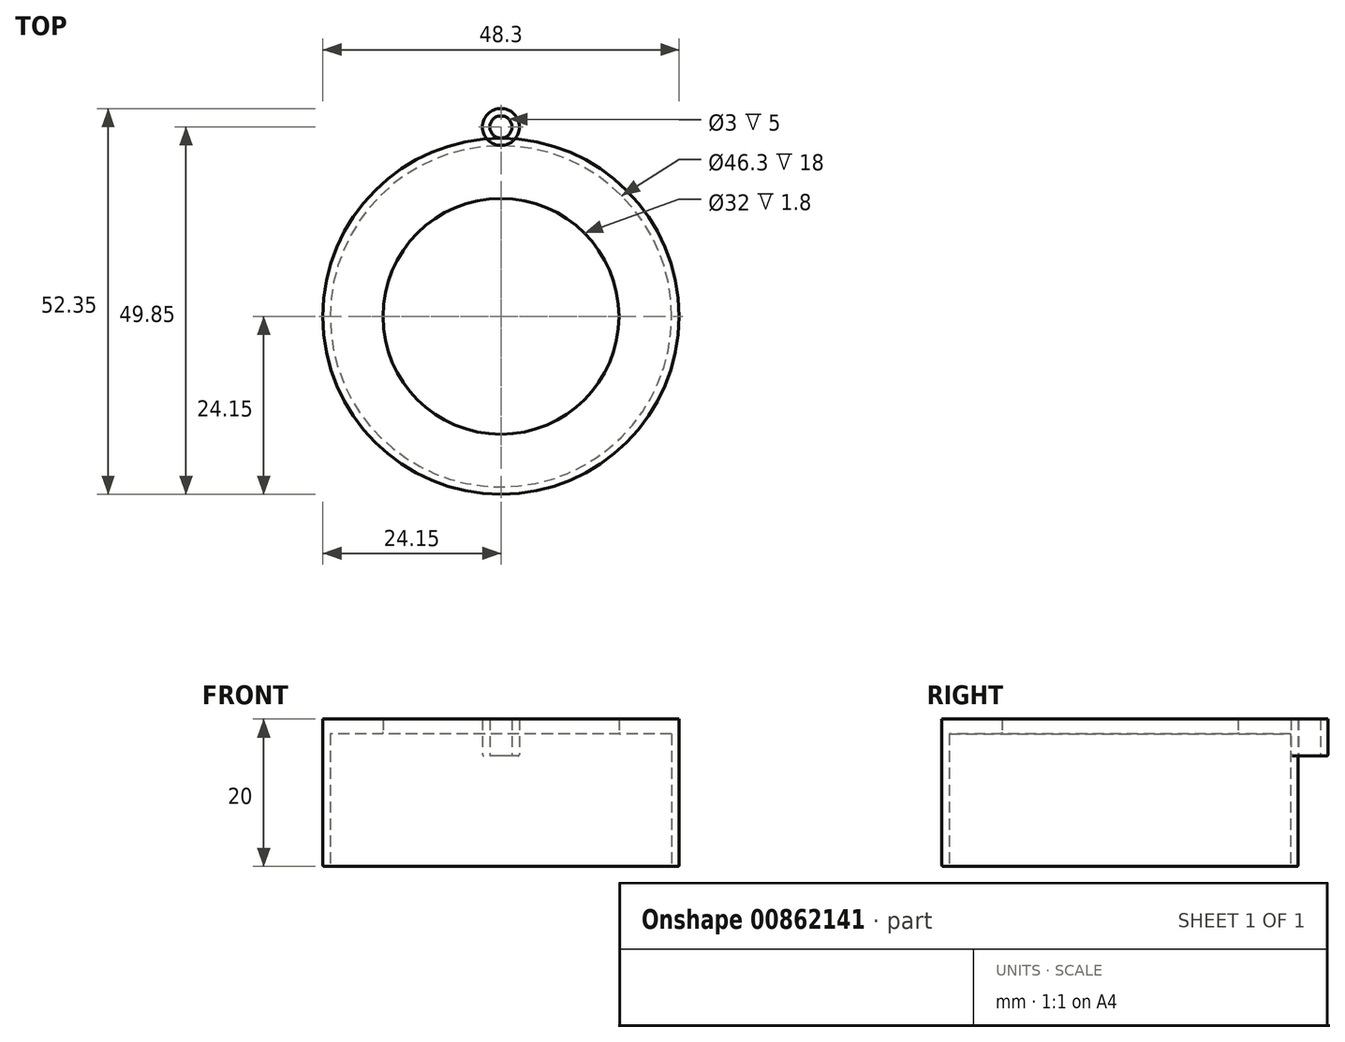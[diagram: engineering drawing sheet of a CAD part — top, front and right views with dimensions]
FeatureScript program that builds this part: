
annotation { "Feature Type Name" : "Feature", "Feature Type Description" : "" }
export const myFeature = defineFeature(function(context is Context, id is Id, definition is map)
    precondition{}
    {
        {
            var Q0;
            Q0=qCreatedBy(makeId("Top.planeOp"),FACE);
            var sketch = newSketch(context, id + "F0", { "sketchPlane" : qUnion([Q0])});
            skCircle(sketch, "E0", {"center": v(0, 0) * mm, "radius": 24.15 * mm});
            skSolve(sketch);
        }
        {
            var Q0;
            Q0 = qSketchRegion(id + "F0", true);
            extrude(context, id + "F1", {"entities" : qUnion([Q0]), "depth" : 20 * mm, "offsetDistance" : 25 * mm});
        }
        {
            var Q0;
            Q0=qCreatedBy(makeId("Top.planeOp"),FACE);
            var sketch = newSketch(context, id + "F2", { "sketchPlane" : qUnion([Q0])});
            skCircle(sketch, "E1", {"center": v(0, 0) * mm, "radius": 23.15 * mm});
            skSolve(sketch);
        }
        {
            var Q0;
            Q0 = qSketchRegion(id + "F2", true);
            extrude(context, id + "F3", {"entities" : qUnion([Q0]), "operationType" : NewBodyOperationType.REMOVE, "depth" : 18 * mm, "offsetDistance" : 25 * mm});
        }
        {
            var Q0;
            Q0=qCreatedBy(makeId("Top.planeOp"),FACE);
            var sketch = newSketch(context, id + "F4", { "sketchPlane" : qUnion([Q0])});
            skCircle(sketch, "E2", {"center": v(0, 0) * mm, "radius": 16 * mm});
            skSolve(sketch);
        }
        {
            var Q0;
            Q0 = qSketchRegion(id + "F4", true);
            extrude(context, id + "F5", {"entities" : qUnion([Q0]), "operationType" : NewBodyOperationType.REMOVE, "depth" : 20 * mm, "offsetDistance" : 25 * mm});
        }
        {
            var Q0;
            Q0=qCreatedBy(makeId("Top.planeOp"),FACE);
            var sketch = newSketch(context, id + "F6", { "sketchPlane" : qUnion([Q0])});
            skCircle(sketch, "E3", {"center": v(0, 0) * mm, "radius": 2.5 * mm});
            skSolve(sketch);
        }
        {
            var Q0;
            Q0 = qSketchRegion(id + "F6", true);
            extrude(context, id + "F7", {"entities" : qUnion([Q0]), "depth" : 5 * mm, "offsetDistance" : 25 * mm});
        }
        {
            var Q0;
            Q0=qCreatedBy(makeId("Top.planeOp"),FACE);
            var sketch = newSketch(context, id + "F8", { "sketchPlane" : qUnion([Q0])});
            skCircle(sketch, "E4", {"center": v(0, 0) * mm, "radius": 1.5 * mm});
            skSolve(sketch);
        }
        {
            var Q0;
            Q0 = qSketchRegion(id + "F8", true);
            extrude(context, id + "F9", {"entities" : qUnion([Q0]), "operationType" : NewBodyOperationType.REMOVE, "depth" : 5 * mm, "offsetDistance" : 25 * mm});
        }
        {
            var Q0;
            Q0=makeQuery(id+"F7.opExtrude","SWEPT_BODY",BODY,{"disambiguationData":[OSD([sQuery(id+"F6.wireOp",EDGE,"E3")])]});
            transform(context, id + "F10", {"entities" : qUnion([Q0]), "transformType" : TransformType.TRANSLATION_3D, "dx" : 0 * mm, "dy" : 25.6 * mm, "dz" : 15 * mm, "makeCopy" : false});
        }
        {
            var Q0;
            Q0=makeQuery(id+"F1.opExtrude","CAP_EDGE",EDGE,{"disambiguationData":[OSD([sQuery(id+"F0.wireOp",EDGE,"E0")])],"isStart":true});
            var Q1;
            Q1=makeQuery(id+"F3.boolean.opBoolean","COPY",EDGE,{"derivedFrom":makeQuery(id+"F3.opExtrude","CAP_EDGE",EDGE,{"disambiguationData":[OSD([sQuery(id+"F2.wireOp",EDGE,"E1")])],"isStart":true})});
            var Q2;
            Q2=makeQuery(id+"F5.boolean.opBoolean","INTERSECT",EDGE,{"derivedFrom":[makeQuery(id+"F3.boolean.opBoolean","COPY",FACE,{"derivedFrom":makeQuery(id+"F3.opExtrude","CAP_FACE",FACE,{"disambiguationData":[OSD([sQuery(id+"F2.wireOp",EDGE,"E1")])],"isStart":false})}),makeQuery(id+"F5.opExtrude","SWEPT_FACE",FACE,{"disambiguationData":[OSD([sQuery(id+"F4.wireOp",EDGE,"E2")])]})]});
            var Q3;
            Q3=makeQuery(id+"F7.opExtrude","CAP_EDGE",EDGE,{"disambiguationData":[OSD([sQuery(id+"F6.wireOp",EDGE,"E3")])],"isStart":true});
            var Q4;
            Q4=makeQuery(id+"F9.boolean.opBoolean","COPY",EDGE,{"derivedFrom":makeQuery(id+"F9.opExtrude","CAP_EDGE",EDGE,{"disambiguationData":[OSD([sQuery(id+"F8.wireOp",EDGE,"E4")])],"isStart":true})});
            fillet(context, id + "F11", {"entities" : qUnion([Q0, Q1, Q2, Q3, Q4]), "radius" : 0.2 * mm, "tangentPropagation" : true, "allowEdgeOverflow" : false});
        }
        {
            var Q0;
            Q0=makeQuery(id+"F7.opExtrude","SWEPT_BODY",BODY,{"disambiguationData":[OSD([sQuery(id+"F6.wireOp",EDGE,"E3")])]});
            transform(context, id + "F12", {"entities" : qUnion([Q0]), "transformType" : TransformType.TRANSLATION_3D, "dx" : 0 * mm, "dy" : 0.1 * mm, "dz" : 0 * mm, "makeCopy" : false});
        }
    });
